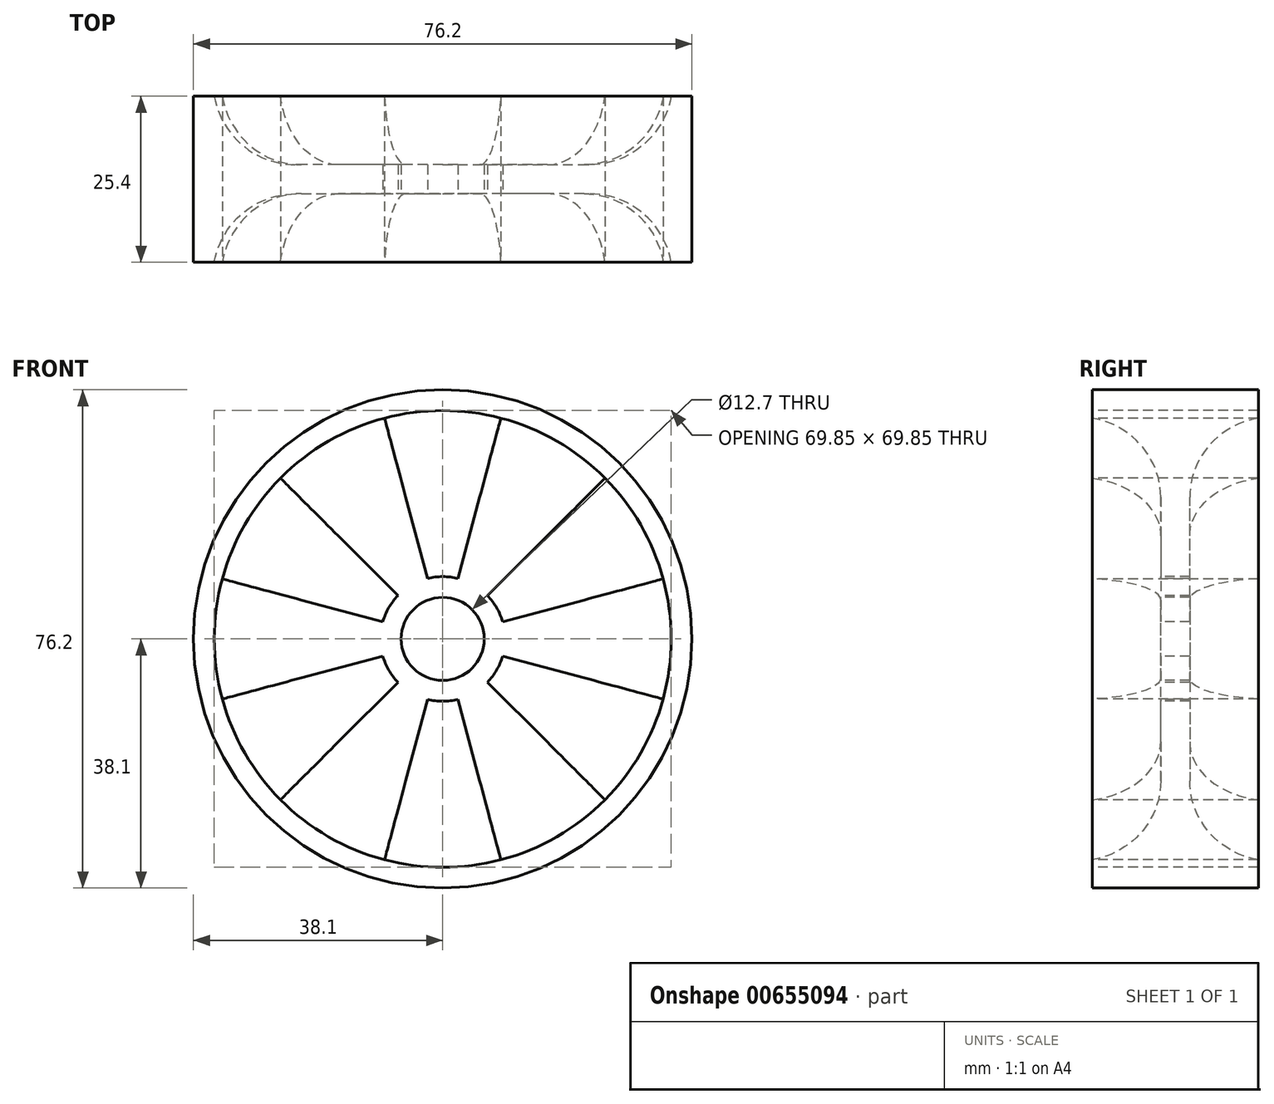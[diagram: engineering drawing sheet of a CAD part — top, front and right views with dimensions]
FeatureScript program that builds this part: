
annotation { "Feature Type Name" : "Feature", "Feature Type Description" : "" }
export const myFeature = defineFeature(function(context is Context, id is Id, definition is map)
    precondition{}
    {
        {
            var Q0;
            Q0=qCreatedBy(makeId("Front.planeOp"),FACE);
            var sketch = newSketch(context, id + "F0", { "sketchPlane" : qUnion([Q0])});
            skCircle(sketch, "E0", {"center": v(0, 0) * mm, "radius": 38.1 * mm});
            skSolve(sketch);
        }
        {
            var Q0;
            Q0 = qSketchRegion(id + "F0", true);
            extrude(context, id + "F1", {"entities" : qUnion([Q0]), "depth" : 12.7 * mm, "offsetDistance" : 25.4 * mm, "hasSecondDirection" : true, "secondDirectionOppositeDirection" : true, "secondDirectionDepth" : 12.7 * mm});
        }
        {
            var Q0;
            Q0=qCreatedBy(makeId("Front.planeOp"),FACE);
            var sketch = newSketch(context, id + "F2", { "sketchPlane" : qUnion([Q0])});
            skArc(sketch, "E1", {"start": v(-9.16, -2.61) * mm, "mid": v(-8.25, -4.76) * mm, "end": v(-6.84, -6.63) * mm});
            skArc(sketch, "E2", {"start": v(-24.8, 24.59) * mm, "mid": v(-30.25, 17.46) * mm, "end": v(-33.7, 9.19) * mm});
            skLineSegment(sketch, "E3", {"start": v(-2.32, 9.24) * mm, "end": v(-8.9, 33.77) * mm});
            skLineSegment(sketch, "E4", {"start": v(2.32, 9.24) * mm, "end": v(8.9, 33.77) * mm});
            skLineSegment(sketch, "E5.1.0", {"start": v(-9.16, 2.61) * mm, "end": v(-33.7, 9.19) * mm});
            skLineSegment(sketch, "E5.1.1", {"start": v(-6.84, 6.63) * mm, "end": v(-24.8, 24.59) * mm});
            skLineSegment(sketch, "E5.2.0", {"start": v(-6.84, -6.63) * mm, "end": v(-24.8, -24.59) * mm});
            skLineSegment(sketch, "E5.2.1", {"start": v(-9.16, -2.61) * mm, "end": v(-33.7, -9.19) * mm});
            skLineSegment(sketch, "E5.3.0", {"start": v(2.32, -9.24) * mm, "end": v(8.89, -33.77) * mm});
            skLineSegment(sketch, "E5.3.1", {"start": v(-2.32, -9.24) * mm, "end": v(-8.9, -33.77) * mm});
            skLineSegment(sketch, "E5.4.0", {"start": v(9.16, -2.61) * mm, "end": v(33.7, -9.19) * mm});
            skLineSegment(sketch, "E5.4.1", {"start": v(6.84, -6.63) * mm, "end": v(24.8, -24.59) * mm});
            skLineSegment(sketch, "E6.1.5.0", {"start": v(6.84, 6.63) * mm, "end": v(24.8, 24.59) * mm});
            skLineSegment(sketch, "E6.3.5.0", {"start": v(9.16, 2.61) * mm, "end": v(33.7, 9.19) * mm});
            skArc(sketch, "E7.trimOffspring", {"start": v(8.9, 33.77) * mm, "mid": v(0, 34.93) * mm, "end": v(-8.89, 33.77) * mm});
            skArc(sketch, "E8.trimOffspring", {"start": v(33.7, 9.19) * mm, "mid": v(30.25, 17.46) * mm, "end": v(24.8, 24.59) * mm});
            skArc(sketch, "E9.trimOffspring", {"start": v(24.8, -24.59) * mm, "mid": v(30.25, -17.46) * mm, "end": v(33.7, -9.19) * mm});
            skArc(sketch, "E10.trimOffspring", {"start": v(-8.89, -33.77) * mm, "mid": v(0, -34.93) * mm, "end": v(8.89, -33.77) * mm});
            skArc(sketch, "E11.trimOffspring", {"start": v(-33.7, -9.19) * mm, "mid": v(-30.25, -17.46) * mm, "end": v(-24.8, -24.59) * mm});
            skCircle(sketch, "E12", {"center": v(0, 0) * mm, "radius": 6.35 * mm});
            skArc(sketch, "E13.trimOffspring", {"start": v(-6.84, 6.63) * mm, "mid": v(-8.25, 4.76) * mm, "end": v(-9.16, 2.61) * mm});
            skArc(sketch, "E14.trimOffspring", {"start": v(2.32, 9.24) * mm, "mid": v(0, 9.53) * mm, "end": v(-2.32, 9.24) * mm});
            skArc(sketch, "E15.trimOffspring", {"start": v(9.16, 2.61) * mm, "mid": v(8.25, 4.76) * mm, "end": v(6.84, 6.63) * mm});
            skArc(sketch, "E16.trimOffspring", {"start": v(6.84, -6.63) * mm, "mid": v(8.25, -4.76) * mm, "end": v(9.16, -2.61) * mm});
            skArc(sketch, "E17.trimOffspring", {"start": v(-2.32, -9.24) * mm, "mid": v(0, -9.53) * mm, "end": v(2.32, -9.24) * mm});
            skSolve(sketch);
        }
        {
            var Q0;
            Q0 = qSketchRegion(id + "F2", true);
            extrude(context, id + "F3", {"entities" : qUnion([Q0]), "operationType" : NewBodyOperationType.REMOVE, "oppositeDirection" : true, "depth" : 25.4 * mm, "offsetDistance" : 25.4 * mm, "hasSecondDirection" : true, "secondDirectionOppositeDirection" : false, "secondDirectionDepth" : 25.4 * mm});
        }
        {
            var Q0;
            Q0=makeQuery(id+"F1.opExtrude","CAP_FACE",FACE,{"disambiguationData":[OSD([sQuery(id+"F0.wireOp",EDGE,"E0")])],"isStart":false});
            var sketch = newSketch(context, id + "F4", { "sketchPlane" : qUnion([Q0])});
            skCircle(sketch, "E18", {"center": v(0, 0) * mm, "radius": 34.93 * mm});
            skSolve(sketch);
        }
        {
            var Q0;
            Q0 = qSketchRegion(id + "F4", true);
            extrude(context, id + "F5", {"entities" : qUnion([Q0]), "operationType" : NewBodyOperationType.REMOVE, "oppositeDirection" : true, "depth" : 10.48 * mm, "offsetDistance" : 25.4 * mm});
        }
        {
            var Q0;
            Q0=makeQuery(id+"F1.opExtrude","CAP_FACE",FACE,{"disambiguationData":[OSD([sQuery(id+"F0.wireOp",EDGE,"E0")])],"isStart":true});
            var sketch = newSketch(context, id + "F6", { "sketchPlane" : qUnion([Q0])});
            skCircle(sketch, "E19", {"center": v(0, 0) * mm, "radius": 34.93 * mm});
            skSolve(sketch);
        }
        {
            var Q0;
            Q0 = qSketchRegion(id + "F6", true);
            extrude(context, id + "F7", {"entities" : qUnion([Q0]), "operationType" : NewBodyOperationType.REMOVE, "oppositeDirection" : true, "depth" : 10.48 * mm, "offsetDistance" : 25.4 * mm});
        }
        {
            var Q0;
            {var subQ0=sQuery(id+"F4.wireOp",EDGE,"E18");Q0=makeQuery(id+"F5.boolean.opBoolean","COPY",EDGE,{"disambiguationData":[TD([makeQuery(id+"F3.boolean.opBoolean","COPY",FACE,{"derivedFrom":makeQuery(id+"F3.opExtrude","SWEPT_FACE",FACE,{"disambiguationData":[OSD([sQuery(id+"F2.wireOp",EDGE,"E5.3.0")])]})})])],"derivedFrom":makeQuery(id+"F5.opExtrude","CAP_EDGE",EDGE,{"disambiguationData":[OSD([subQ0])],"isStart":false})});}
            var Q1;
            {var subQ0=sQuery(id+"F4.wireOp",EDGE,"E18");Q1=makeQuery(id+"F5.boolean.opBoolean","COPY",EDGE,{"disambiguationData":[TD([makeQuery(id+"F3.boolean.opBoolean","COPY",FACE,{"derivedFrom":makeQuery(id+"F3.opExtrude","SWEPT_FACE",FACE,{"disambiguationData":[OSD([sQuery(id+"F2.wireOp",EDGE,"E5.2.0")])]})})])],"derivedFrom":makeQuery(id+"F5.opExtrude","CAP_EDGE",EDGE,{"disambiguationData":[OSD([subQ0])],"isStart":false})});}
            var Q2;
            {var subQ0=sQuery(id+"F4.wireOp",EDGE,"E18");Q2=makeQuery(id+"F5.boolean.opBoolean","COPY",EDGE,{"disambiguationData":[TD([makeQuery(id+"F3.boolean.opBoolean","COPY",FACE,{"derivedFrom":makeQuery(id+"F3.opExtrude","SWEPT_FACE",FACE,{"disambiguationData":[OSD([sQuery(id+"F2.wireOp",EDGE,"E5.1.0")])]})})])],"derivedFrom":makeQuery(id+"F5.opExtrude","CAP_EDGE",EDGE,{"disambiguationData":[OSD([subQ0])],"isStart":false})});}
            var Q3;
            {var subQ0=sQuery(id+"F4.wireOp",EDGE,"E18");Q3=makeQuery(id+"F5.boolean.opBoolean","COPY",EDGE,{"disambiguationData":[TD([makeQuery(id+"F3.boolean.opBoolean","COPY",FACE,{"derivedFrom":makeQuery(id+"F3.opExtrude","SWEPT_FACE",FACE,{"disambiguationData":[OSD([sQuery(id+"F2.wireOp",EDGE,"E3")])]})})])],"derivedFrom":makeQuery(id+"F5.opExtrude","CAP_EDGE",EDGE,{"disambiguationData":[OSD([subQ0])],"isStart":false})});}
            var Q4;
            {var subQ0=sQuery(id+"F4.wireOp",EDGE,"E18");Q4=makeQuery(id+"F5.boolean.opBoolean","COPY",EDGE,{"disambiguationData":[TD([makeQuery(id+"F3.boolean.opBoolean","COPY",FACE,{"derivedFrom":makeQuery(id+"F3.opExtrude","SWEPT_FACE",FACE,{"disambiguationData":[OSD([sQuery(id+"F2.wireOp",EDGE,"E4")])]})})])],"derivedFrom":makeQuery(id+"F5.opExtrude","CAP_EDGE",EDGE,{"disambiguationData":[OSD([subQ0])],"isStart":false})});}
            var Q5;
            {var subQ0=sQuery(id+"F4.wireOp",EDGE,"E18");Q5=makeQuery(id+"F5.boolean.opBoolean","COPY",EDGE,{"disambiguationData":[TD([makeQuery(id+"F3.boolean.opBoolean","COPY",FACE,{"derivedFrom":makeQuery(id+"F3.opExtrude","SWEPT_FACE",FACE,{"disambiguationData":[OSD([sQuery(id+"F2.wireOp",EDGE,"E5.4.0")])]})})])],"derivedFrom":makeQuery(id+"F5.opExtrude","CAP_EDGE",EDGE,{"disambiguationData":[OSD([subQ0])],"isStart":false})});}
            var Q6;
            {var subQ0=sQuery(id+"F6.wireOp",EDGE,"E19");Q6=makeQuery(id+"F7.boolean.opBoolean","COPY",EDGE,{"disambiguationData":[TD([makeQuery(id+"F3.boolean.opBoolean","COPY",FACE,{"derivedFrom":makeQuery(id+"F3.opExtrude","SWEPT_FACE",FACE,{"disambiguationData":[OSD([sQuery(id+"F2.wireOp",EDGE,"E3")])]})})])],"derivedFrom":makeQuery(id+"F7.opExtrude","CAP_EDGE",EDGE,{"disambiguationData":[OSD([subQ0])],"isStart":false})});}
            var Q7;
            {var subQ0=sQuery(id+"F6.wireOp",EDGE,"E19");Q7=makeQuery(id+"F7.boolean.opBoolean","COPY",EDGE,{"disambiguationData":[TD([makeQuery(id+"F3.boolean.opBoolean","COPY",FACE,{"derivedFrom":makeQuery(id+"F3.opExtrude","SWEPT_FACE",FACE,{"disambiguationData":[OSD([sQuery(id+"F2.wireOp",EDGE,"E5.1.0")])]})})])],"derivedFrom":makeQuery(id+"F7.opExtrude","CAP_EDGE",EDGE,{"disambiguationData":[OSD([subQ0])],"isStart":false})});}
            var Q8;
            {var subQ0=sQuery(id+"F6.wireOp",EDGE,"E19");Q8=makeQuery(id+"F7.boolean.opBoolean","COPY",EDGE,{"disambiguationData":[TD([makeQuery(id+"F3.boolean.opBoolean","COPY",FACE,{"derivedFrom":makeQuery(id+"F3.opExtrude","SWEPT_FACE",FACE,{"disambiguationData":[OSD([sQuery(id+"F2.wireOp",EDGE,"E4")])]})})])],"derivedFrom":makeQuery(id+"F7.opExtrude","CAP_EDGE",EDGE,{"disambiguationData":[OSD([subQ0])],"isStart":false})});}
            var Q9;
            {var subQ0=sQuery(id+"F6.wireOp",EDGE,"E19");Q9=makeQuery(id+"F7.boolean.opBoolean","COPY",EDGE,{"disambiguationData":[TD([makeQuery(id+"F3.boolean.opBoolean","COPY",FACE,{"derivedFrom":makeQuery(id+"F3.opExtrude","SWEPT_FACE",FACE,{"disambiguationData":[OSD([sQuery(id+"F2.wireOp",EDGE,"E5.3.0")])]})})])],"derivedFrom":makeQuery(id+"F7.opExtrude","CAP_EDGE",EDGE,{"disambiguationData":[OSD([subQ0])],"isStart":false})});}
            var Q10;
            {var subQ0=sQuery(id+"F6.wireOp",EDGE,"E19");Q10=makeQuery(id+"F7.boolean.opBoolean","COPY",EDGE,{"disambiguationData":[TD([makeQuery(id+"F3.boolean.opBoolean","COPY",FACE,{"derivedFrom":makeQuery(id+"F3.opExtrude","SWEPT_FACE",FACE,{"disambiguationData":[OSD([sQuery(id+"F2.wireOp",EDGE,"E5.2.0")])]})})])],"derivedFrom":makeQuery(id+"F7.opExtrude","CAP_EDGE",EDGE,{"disambiguationData":[OSD([subQ0])],"isStart":false})});}
            var Q11;
            {var subQ0=sQuery(id+"F6.wireOp",EDGE,"E19");Q11=makeQuery(id+"F7.boolean.opBoolean","COPY",EDGE,{"disambiguationData":[TD([makeQuery(id+"F3.boolean.opBoolean","COPY",FACE,{"derivedFrom":makeQuery(id+"F3.opExtrude","SWEPT_FACE",FACE,{"disambiguationData":[OSD([sQuery(id+"F2.wireOp",EDGE,"E5.4.0")])]})})])],"derivedFrom":makeQuery(id+"F7.opExtrude","CAP_EDGE",EDGE,{"disambiguationData":[OSD([subQ0])],"isStart":false})});}
            fillet(context, id + "F8", {"entities" : qUnion([Q0, Q1, Q2, Q3, Q4, Q5, Q6, Q7, Q8, Q9, Q10, Q11]), "radius" : 12.7 * mm, "tangentPropagation" : true, "allowEdgeOverflow" : false});
        }
    });
